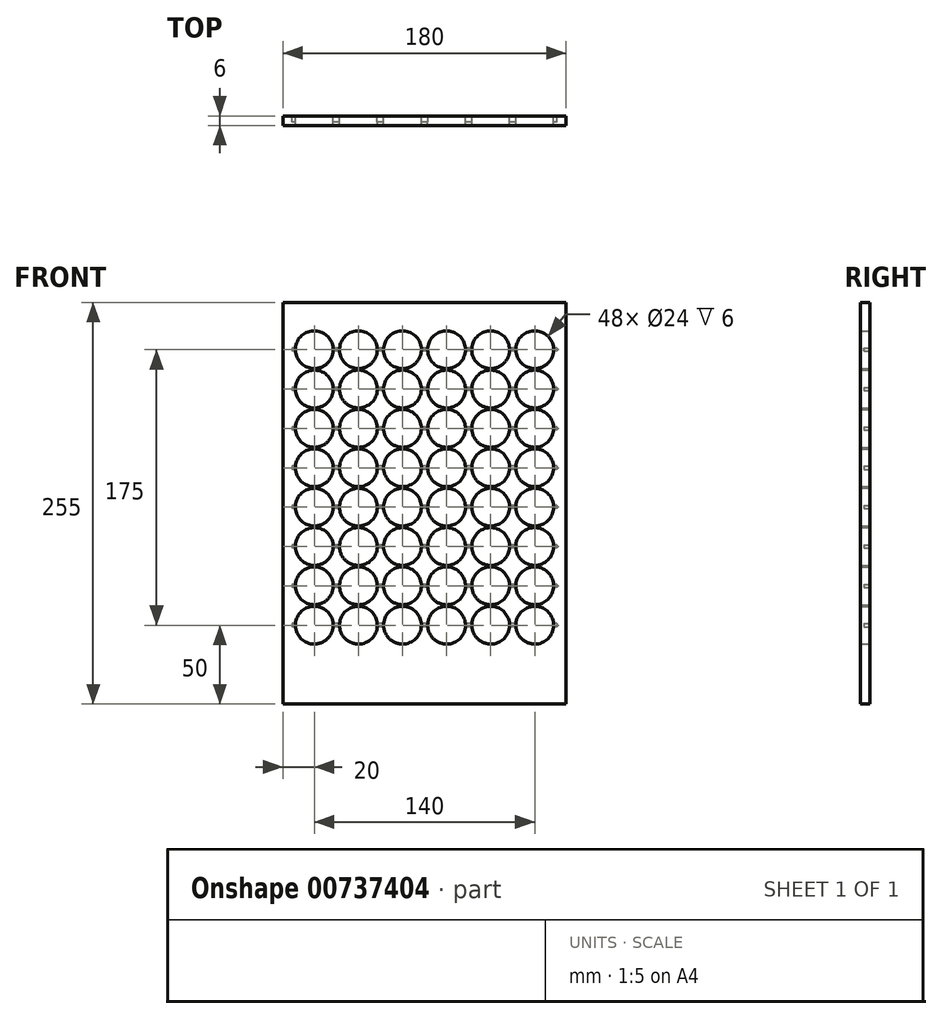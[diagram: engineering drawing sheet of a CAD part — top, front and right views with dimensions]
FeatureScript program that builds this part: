
annotation { "Feature Type Name" : "Feature", "Feature Type Description" : "" }
export const myFeature = defineFeature(function(context is Context, id is Id, definition is map)
    precondition{}
    {
        {
            var Q0;
            Q0=qCreatedBy(makeId("Front.planeOp"),FACE);
            var sketch = newSketch(context, id + "F0", { "sketchPlane" : qUnion([Q0])});
            skLineSegment(sketch, "E0.bottom", {"start": v(90, -127.5) * mm, "end": v(-90, -127.5) * mm});
            skLineSegment(sketch, "E0.top", {"start": v(90, 127.5) * mm, "end": v(-90, 127.5) * mm});
            skLineSegment(sketch, "E0.left", {"start": v(90, -127.5) * mm, "end": v(90, 127.5) * mm});
            skLineSegment(sketch, "E0.right", {"start": v(-90, -127.5) * mm, "end": v(-90, 127.5) * mm});
            skPoint(sketch, "E0.middle", {"position": v(0, 0) * mm});
            skLineSegment(sketch, "E1", {"start": v(-90, 97.5) * mm, "end": v(90, 97.5) * mm, "construction": true});
            skCircle(sketch, "E2", {"center": v(-70, 97.5) * mm, "radius": 12 * mm});
            skCircle(sketch, "E3.0.1.0", {"center": v(-70, 72.5) * mm, "radius": 12 * mm});
            skCircle(sketch, "E3.0.2.0", {"center": v(-70, 47.5) * mm, "radius": 12 * mm});
            skCircle(sketch, "E3.0.3.0", {"center": v(-70, 22.5) * mm, "radius": 12 * mm});
            skCircle(sketch, "E3.0.4.0", {"center": v(-70, -2.5) * mm, "radius": 12 * mm});
            skCircle(sketch, "E3.0.5.0", {"center": v(-70, -27.5) * mm, "radius": 12 * mm});
            skCircle(sketch, "E3.0.6.0", {"center": v(-70, -52.5) * mm, "radius": 12 * mm});
            skCircle(sketch, "E3.0.7.0", {"center": v(-70, -77.5) * mm, "radius": 12 * mm});
            skCircle(sketch, "E3.1.0.0", {"center": v(-42, 97.5) * mm, "radius": 12 * mm});
            skCircle(sketch, "E3.1.1.0", {"center": v(-42, 72.5) * mm, "radius": 12 * mm});
            skCircle(sketch, "E3.1.2.0", {"center": v(-42, 47.5) * mm, "radius": 12 * mm});
            skCircle(sketch, "E3.1.3.0", {"center": v(-42, 22.5) * mm, "radius": 12 * mm});
            skCircle(sketch, "E3.1.4.0", {"center": v(-42, -2.5) * mm, "radius": 12 * mm});
            skCircle(sketch, "E3.1.5.0", {"center": v(-42, -27.5) * mm, "radius": 12 * mm});
            skCircle(sketch, "E3.1.6.0", {"center": v(-42, -52.5) * mm, "radius": 12 * mm});
            skCircle(sketch, "E3.1.7.0", {"center": v(-42, -77.5) * mm, "radius": 12 * mm});
            skCircle(sketch, "E3.2.0.0", {"center": v(-14, 97.5) * mm, "radius": 12 * mm});
            skCircle(sketch, "E3.2.1.0", {"center": v(-14, 72.5) * mm, "radius": 12 * mm});
            skCircle(sketch, "E3.2.2.0", {"center": v(-14, 47.5) * mm, "radius": 12 * mm});
            skCircle(sketch, "E3.2.3.0", {"center": v(-14, 22.5) * mm, "radius": 12 * mm});
            skCircle(sketch, "E3.2.4.0", {"center": v(-14, -2.5) * mm, "radius": 12 * mm});
            skCircle(sketch, "E3.2.5.0", {"center": v(-14, -27.5) * mm, "radius": 12 * mm});
            skCircle(sketch, "E3.2.6.0", {"center": v(-14, -52.5) * mm, "radius": 12 * mm});
            skCircle(sketch, "E3.2.7.0", {"center": v(-14, -77.5) * mm, "radius": 12 * mm});
            skCircle(sketch, "E3.3.0.0", {"center": v(14, 97.5) * mm, "radius": 12 * mm});
            skCircle(sketch, "E3.3.1.0", {"center": v(14, 72.5) * mm, "radius": 12 * mm});
            skCircle(sketch, "E3.3.2.0", {"center": v(14, 47.5) * mm, "radius": 12 * mm});
            skCircle(sketch, "E3.3.3.0", {"center": v(14, 22.5) * mm, "radius": 12 * mm});
            skCircle(sketch, "E3.3.4.0", {"center": v(14, -2.5) * mm, "radius": 12 * mm});
            skCircle(sketch, "E3.3.5.0", {"center": v(14, -27.5) * mm, "radius": 12 * mm});
            skCircle(sketch, "E3.3.6.0", {"center": v(14, -52.5) * mm, "radius": 12 * mm});
            skCircle(sketch, "E3.3.7.0", {"center": v(14, -77.5) * mm, "radius": 12 * mm});
            skCircle(sketch, "E3.4.0.0", {"center": v(42, 97.5) * mm, "radius": 12 * mm});
            skCircle(sketch, "E3.4.1.0", {"center": v(42, 72.5) * mm, "radius": 12 * mm});
            skCircle(sketch, "E3.4.2.0", {"center": v(42, 47.5) * mm, "radius": 12 * mm});
            skCircle(sketch, "E3.4.3.0", {"center": v(42, 22.5) * mm, "radius": 12 * mm});
            skCircle(sketch, "E3.4.4.0", {"center": v(42, -2.5) * mm, "radius": 12 * mm});
            skCircle(sketch, "E3.4.5.0", {"center": v(42, -27.5) * mm, "radius": 12 * mm});
            skCircle(sketch, "E3.4.6.0", {"center": v(42, -52.5) * mm, "radius": 12 * mm});
            skCircle(sketch, "E3.4.7.0", {"center": v(42, -77.5) * mm, "radius": 12 * mm});
            skCircle(sketch, "E3.5.0.0", {"center": v(70, 97.5) * mm, "radius": 12 * mm});
            skCircle(sketch, "E3.5.1.0", {"center": v(70, 72.5) * mm, "radius": 12 * mm});
            skCircle(sketch, "E3.5.2.0", {"center": v(70, 47.5) * mm, "radius": 12 * mm});
            skCircle(sketch, "E3.5.3.0", {"center": v(70, 22.5) * mm, "radius": 12 * mm});
            skCircle(sketch, "E3.5.4.0", {"center": v(70, -2.5) * mm, "radius": 12 * mm});
            skCircle(sketch, "E3.5.5.0", {"center": v(70, -27.5) * mm, "radius": 12 * mm});
            skCircle(sketch, "E3.5.6.0", {"center": v(70, -52.5) * mm, "radius": 12 * mm});
            skCircle(sketch, "E3.5.7.0", {"center": v(70, -77.5) * mm, "radius": 12 * mm});
            skLineSegment(sketch, "E3.direction1", {"start": v(-70, 97.5) * mm, "end": v(-42, 97.5) * mm, "construction": true});
            skLineSegment(sketch, "E3.direction2", {"start": v(-70, 97.5) * mm, "end": v(-70, 72.5) * mm, "construction": true});
            skSolve(sketch);
        }
        {
            var Q0;
            Q0 = qSketchRegion(id + "F0", true);
            var Q1;
            Q1 = qSketchRegion(id + "F2", true);
            extrude(context, id + "F1", {"entities" : qUnion([Q0, Q1]), "depth" : 6 * mm, "offsetDistance" : 25 * mm});
        }
        {
            var Q0;
            Q0=makeQuery(id+"F1.opExtrude","CAP_FACE",FACE,{"disambiguationData":[OSD([sQuery(id+"F0.wireOp",EDGE,"E0.bottom"),sQuery(id+"F0.wireOp",EDGE,"E0.top"),sQuery(id+"F0.wireOp",EDGE,"E0.left"),sQuery(id+"F0.wireOp",EDGE,"E0.right"),sQuery(id+"F0.wireOp",EDGE,"E2"),sQuery(id+"F0.wireOp",EDGE,"E3.0.1.0"),sQuery(id+"F0.wireOp",EDGE,"E3.0.2.0"),sQuery(id+"F0.wireOp",EDGE,"E3.0.3.0"),sQuery(id+"F0.wireOp",EDGE,"E3.0.4.0"),sQuery(id+"F0.wireOp",EDGE,"E3.0.5.0"),sQuery(id+"F0.wireOp",EDGE,"E3.0.6.0"),sQuery(id+"F0.wireOp",EDGE,"E3.0.7.0"),sQuery(id+"F0.wireOp",EDGE,"E3.1.0.0"),sQuery(id+"F0.wireOp",EDGE,"E3.1.1.0"),sQuery(id+"F0.wireOp",EDGE,"E3.1.2.0"),sQuery(id+"F0.wireOp",EDGE,"E3.1.3.0"),sQuery(id+"F0.wireOp",EDGE,"E3.1.4.0"),sQuery(id+"F0.wireOp",EDGE,"E3.1.5.0"),sQuery(id+"F0.wireOp",EDGE,"E3.1.6.0"),sQuery(id+"F0.wireOp",EDGE,"E3.1.7.0"),sQuery(id+"F0.wireOp",EDGE,"E3.2.0.0"),sQuery(id+"F0.wireOp",EDGE,"E3.2.1.0"),sQuery(id+"F0.wireOp",EDGE,"E3.2.2.0"),sQuery(id+"F0.wireOp",EDGE,"E3.2.3.0"),sQuery(id+"F0.wireOp",EDGE,"E3.2.4.0"),sQuery(id+"F0.wireOp",EDGE,"E3.2.5.0"),sQuery(id+"F0.wireOp",EDGE,"E3.2.6.0"),sQuery(id+"F0.wireOp",EDGE,"E3.2.7.0"),sQuery(id+"F0.wireOp",EDGE,"E3.3.0.0"),sQuery(id+"F0.wireOp",EDGE,"E3.3.1.0"),sQuery(id+"F0.wireOp",EDGE,"E3.3.2.0"),sQuery(id+"F0.wireOp",EDGE,"E3.3.3.0"),sQuery(id+"F0.wireOp",EDGE,"E3.3.4.0"),sQuery(id+"F0.wireOp",EDGE,"E3.3.5.0"),sQuery(id+"F0.wireOp",EDGE,"E3.3.6.0"),sQuery(id+"F0.wireOp",EDGE,"E3.3.7.0"),sQuery(id+"F0.wireOp",EDGE,"E3.4.0.0"),sQuery(id+"F0.wireOp",EDGE,"E3.4.1.0"),sQuery(id+"F0.wireOp",EDGE,"E3.4.2.0"),sQuery(id+"F0.wireOp",EDGE,"E3.4.3.0"),sQuery(id+"F0.wireOp",EDGE,"E3.4.4.0"),sQuery(id+"F0.wireOp",EDGE,"E3.4.5.0"),sQuery(id+"F0.wireOp",EDGE,"E3.4.6.0"),sQuery(id+"F0.wireOp",EDGE,"E3.4.7.0"),sQuery(id+"F0.wireOp",EDGE,"E3.5.0.0"),sQuery(id+"F0.wireOp",EDGE,"E3.5.1.0"),sQuery(id+"F0.wireOp",EDGE,"E3.5.2.0"),sQuery(id+"F0.wireOp",EDGE,"E3.5.3.0"),sQuery(id+"F0.wireOp",EDGE,"E3.5.4.0"),sQuery(id+"F0.wireOp",EDGE,"E3.5.5.0"),sQuery(id+"F0.wireOp",EDGE,"E3.5.6.0"),sQuery(id+"F0.wireOp",EDGE,"E3.5.7.0")])],"isStart":true});
            var sketch = newSketch(context, id + "F2", { "sketchPlane" : qUnion([Q0])});
            skLineSegment(sketch, "E4", {"start": v(-70, 115) * mm, "end": v(-70, -85.73) * mm, "construction": true});
            skLineSegment(sketch, "E5", {"start": v(-70, 97.5) * mm, "end": v(-70, 109.5) * mm, "construction": true});
            skLineSegment(sketch, "E6", {"start": v(-70, 10.5) * mm, "end": v(-70, 9.5) * mm});
            skLineSegment(sketch, "E7", {"start": v(-70, 9.5) * mm, "end": v(-70, 10) * mm});
            skLineSegment(sketch, "E8", {"start": v(-71.62, 10) * mm, "end": v(-70, 10) * mm});
            skLineSegment(sketch, "E9.bottom", {"start": v(-69, 115) * mm, "end": v(-71, 115) * mm});
            skLineSegment(sketch, "E9.top", {"start": v(-69, -95) * mm, "end": v(-71, -95) * mm});
            skLineSegment(sketch, "E9.left", {"start": v(-69, 115) * mm, "end": v(-69, -95) * mm});
            skLineSegment(sketch, "E9.right", {"start": v(-71, 115) * mm, "end": v(-71, -95) * mm});
            skPoint(sketch, "E9.middle", {"position": v(-70, 10) * mm});
            skLineSegment(sketch, "E10.1.0.0", {"start": v(-41, 115) * mm, "end": v(-41, -95) * mm});
            skLineSegment(sketch, "E10.1.0.1", {"start": v(-43, 115) * mm, "end": v(-43, -95) * mm});
            skLineSegment(sketch, "E10.1.0.2", {"start": v(-41, -95) * mm, "end": v(-43, -95) * mm});
            skLineSegment(sketch, "E10.1.0.3", {"start": v(-41, 115) * mm, "end": v(-43, 115) * mm});
            skLineSegment(sketch, "E10.2.0.0", {"start": v(-13, 115) * mm, "end": v(-13, -95) * mm});
            skLineSegment(sketch, "E10.2.0.1", {"start": v(-15, 115) * mm, "end": v(-15, -95) * mm});
            skLineSegment(sketch, "E10.2.0.2", {"start": v(-13, -95) * mm, "end": v(-15, -95) * mm});
            skLineSegment(sketch, "E10.2.0.3", {"start": v(-13, 115) * mm, "end": v(-15, 115) * mm});
            skLineSegment(sketch, "E10.3.0.0", {"start": v(15, 115) * mm, "end": v(15, -95) * mm});
            skLineSegment(sketch, "E10.3.0.1", {"start": v(13, 115) * mm, "end": v(13, -95) * mm});
            skLineSegment(sketch, "E10.3.0.2", {"start": v(15, -95) * mm, "end": v(13, -95) * mm});
            skLineSegment(sketch, "E10.3.0.3", {"start": v(15, 115) * mm, "end": v(13, 115) * mm});
            skLineSegment(sketch, "E10.4.0.0", {"start": v(43, 115) * mm, "end": v(43, -95) * mm});
            skLineSegment(sketch, "E10.4.0.1", {"start": v(41, 115) * mm, "end": v(41, -95) * mm});
            skLineSegment(sketch, "E10.4.0.2", {"start": v(43, -95) * mm, "end": v(41, -95) * mm});
            skLineSegment(sketch, "E10.4.0.3", {"start": v(43, 115) * mm, "end": v(41, 115) * mm});
            skLineSegment(sketch, "E10.5.0.0", {"start": v(71, 115) * mm, "end": v(71, -95) * mm});
            skLineSegment(sketch, "E10.5.0.1", {"start": v(69, 115) * mm, "end": v(69, -95) * mm});
            skLineSegment(sketch, "E10.5.0.2", {"start": v(71, -95) * mm, "end": v(69, -95) * mm});
            skLineSegment(sketch, "E10.5.0.3", {"start": v(71, 115) * mm, "end": v(69, 115) * mm});
            skLineSegment(sketch, "E10.direction1", {"start": v(-71, -95) * mm, "end": v(-43, -95) * mm, "construction": true});
            skSolve(sketch);
        }
        {
            var Q0;
            Q0=makeQuery(id+"F0.imprint","IMPRINT",FACE,{"disambiguationData":[TD([[makeQuery(id+"F0.imprint","IMPRINT",EDGE,{"derivedFrom":sQuery(id+"F0.wireOp",EDGE,"E0.bottom")}),-1.0]])]});
            var sketch = newSketch(context, id + "F3", { "sketchPlane" : qUnion([Q0])});
            skLineSegment(sketch, "E11.bottom", {"start": v(84, 98.5) * mm, "end": v(-84, 98.5) * mm});
            skLineSegment(sketch, "E11.top", {"start": v(84, 96.5) * mm, "end": v(-84, 96.5) * mm});
            skLineSegment(sketch, "E11.left", {"start": v(84, 98.5) * mm, "end": v(84, 96.5) * mm});
            skLineSegment(sketch, "E11.right", {"start": v(-84, 98.5) * mm, "end": v(-84, 96.5) * mm});
            skLineSegment(sketch, "E12.0.1.0", {"start": v(84, 73.5) * mm, "end": v(-84, 73.5) * mm});
            skLineSegment(sketch, "E12.0.1.1", {"start": v(84, 71.5) * mm, "end": v(-84, 71.5) * mm});
            skLineSegment(sketch, "E12.0.1.2", {"start": v(-84, 73.5) * mm, "end": v(-84, 71.5) * mm});
            skLineSegment(sketch, "E12.0.1.3", {"start": v(84, 73.5) * mm, "end": v(84, 71.5) * mm});
            skLineSegment(sketch, "E12.0.2.0", {"start": v(84, 48.5) * mm, "end": v(-84, 48.5) * mm});
            skLineSegment(sketch, "E12.0.2.1", {"start": v(84, 46.5) * mm, "end": v(-84, 46.5) * mm});
            skLineSegment(sketch, "E12.0.2.2", {"start": v(-84, 48.5) * mm, "end": v(-84, 46.5) * mm});
            skLineSegment(sketch, "E12.0.2.3", {"start": v(84, 48.5) * mm, "end": v(84, 46.5) * mm});
            skLineSegment(sketch, "E12.0.3.0", {"start": v(84, 23.5) * mm, "end": v(-84, 23.5) * mm});
            skLineSegment(sketch, "E12.0.3.1", {"start": v(84, 21.5) * mm, "end": v(-84, 21.5) * mm});
            skLineSegment(sketch, "E12.0.3.2", {"start": v(-84, 23.5) * mm, "end": v(-84, 21.5) * mm});
            skLineSegment(sketch, "E12.0.3.3", {"start": v(84, 23.5) * mm, "end": v(84, 21.5) * mm});
            skLineSegment(sketch, "E12.0.4.0", {"start": v(84, -1.5) * mm, "end": v(-84, -1.5) * mm});
            skLineSegment(sketch, "E12.0.4.1", {"start": v(84, -3.5) * mm, "end": v(-84, -3.5) * mm});
            skLineSegment(sketch, "E12.0.4.2", {"start": v(-84, -1.5) * mm, "end": v(-84, -3.5) * mm});
            skLineSegment(sketch, "E12.0.4.3", {"start": v(84, -1.5) * mm, "end": v(84, -3.5) * mm});
            skLineSegment(sketch, "E12.0.5.0", {"start": v(84, -26.5) * mm, "end": v(-84, -26.5) * mm});
            skLineSegment(sketch, "E12.0.5.1", {"start": v(84, -28.5) * mm, "end": v(-84, -28.5) * mm});
            skLineSegment(sketch, "E12.0.5.2", {"start": v(-84, -26.5) * mm, "end": v(-84, -28.5) * mm});
            skLineSegment(sketch, "E12.0.5.3", {"start": v(84, -26.5) * mm, "end": v(84, -28.5) * mm});
            skLineSegment(sketch, "E12.0.6.0", {"start": v(84, -51.5) * mm, "end": v(-84, -51.5) * mm});
            skLineSegment(sketch, "E12.0.6.1", {"start": v(84, -53.5) * mm, "end": v(-84, -53.5) * mm});
            skLineSegment(sketch, "E12.0.6.2", {"start": v(-84, -51.5) * mm, "end": v(-84, -53.5) * mm});
            skLineSegment(sketch, "E12.0.6.3", {"start": v(84, -51.5) * mm, "end": v(84, -53.5) * mm});
            skLineSegment(sketch, "E12.0.7.0", {"start": v(84, -76.5) * mm, "end": v(-84, -76.5) * mm});
            skLineSegment(sketch, "E12.0.7.1", {"start": v(84, -78.5) * mm, "end": v(-84, -78.5) * mm});
            skLineSegment(sketch, "E12.0.7.2", {"start": v(-84, -76.5) * mm, "end": v(-84, -78.5) * mm});
            skLineSegment(sketch, "E12.0.7.3", {"start": v(84, -76.5) * mm, "end": v(84, -78.5) * mm});
            skLineSegment(sketch, "E12.direction1", {"start": v(-84, 98.5) * mm, "end": v(-76, 96) * mm, "construction": true});
            skLineSegment(sketch, "E12.direction2", {"start": v(-84, 98.5) * mm, "end": v(-84, 73.5) * mm, "construction": true});
            skSolve(sketch);
        }
        {
            var Q0;
            Q0 = qSketchRegion(id + "F3", true);
            extrude(context, id + "F4", {"entities" : qUnion([Q0]), "operationType" : NewBodyOperationType.REMOVE, "depth" : 4 * mm, "offsetDistance" : 25 * mm});
        }
    });
